# Revit family: Bitpop C 4.1
name_source: partatom
category: Lighting Fixtures
revit_build: Autodesk Revit 2017 (Build: 20170419_0315(x64)
units: mm (PartAtom-declared; Revit-internal decimal feet)

## family parameters
Always vertical = No
Cut with Voids When Loaded = No
Light Source = Yes
OmniClass Number = 23.80.70.00
OmniClass Title = Lighting
Part Type = Normal
Room Calculation Point = Yes
Round Connector Dimension = Use Diameter
Shared = No
Work Plane-Based = Yes

## types (4) — shared parameters
Apparent Load Phase 1 = 26 W
Body = L&L_White aluminium
CRI = 90 (also available: CRI 80 - ref. URL Technical sheet)
Code = BC4110 B White - Black; BC4110 N Black - Black
Color Filter = 16777215
Control system = on/off; 1-10V + PUSH; DALI + PUSH
Cutout dimensions = -
Default Elevation = 1219 mm
Delivered lumen output = 992 lm (3000K, 30°)
Description = Indoor ceiling mounted
Dimming Lamp Color Temperature Shift = <None>
Emit from Line Length = 610 mm
Energy efficiency class = A A+ A++
Features = -
Geometry = Bitpop C 4.1_mod
Height mm = 100 mm  [stored 0.328084 ft]
IP = 40
LED Colour = 3000K (also available: 2700K and 4000K - ref. URL Technical sheet)
Length mm = 180 mm  [stored 0.590551 ft]
Lens = L&L_Lens
Lumen output at source = 1400 lm (3000K)
Manufacturer = L&L Luce&Light
Material = body in aluminium trim in steel
Model = Bitpop C 4.1
Mounting = surface mounted (ceiling)
No. and type of led = 4 high-intensity power LEDs
Notes = Bitpop 4.1 recessed version
Power = 18W
Power cables = includes 0.3 m cable
Power supply = 230Vac
Power supply unit = included and wired
Tilt Angle = 90.00°
Trim = L&L_Steel
URL = https://www.lucelight.it
URL Accessories and power supply units = https://www.lucelight.it
URL Catalogue = https://www.lucelight.it
URL DXF = https://www.lucelight.it
URL Description = https://www.lucelight.it
URL General code = https://www.lucelight.it
URL IES Photometric file = https://www.lucelight.it
URL Image = https://www.lucelight.it
URL Technical sheet = https://www.lucelight.it
Voltage = 230 V
Weight kg = 0.7
Width mm = 60 mm  [stored 0.19685 ft]
Wiring = -

## per-type parameters (varying)
| type | Optics | Photometric Web File |
| Bitpop C 4.1_F 30° (3000K 18W 230Vac) | 30° | BITPOP C 4.1 F 30° [3000K 18W 230Vac].IES |
| Bitpop C 4.1_L 42° (3000K 18W 230Vac) | 42° | BITPOP C 4.1 L 42° [3000K 18W 230Vac].IES |
| Bitpop C 4.1_W 17°x45° (3000K 18W 230Vac) | 17°x45° | BITPOP C 4.1 W 17°x45° [3000K 18W 230Vac].IES |
| Bitpop C 4.1_S 17° (3000K 18W 230Vac) | 17° | BITPOP C 4.1 S 17° [3000K 18W 230Vac].IES |

note: [stored X ft] marks values corroborated as IEEE doubles in the binary element streams (Revit-internal decimal feet)

## geometry (parser evidence)
native form markers: Blend x2, Sweep x4
no freeform markers — native parametric forms only
